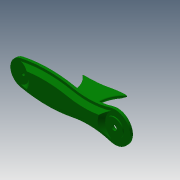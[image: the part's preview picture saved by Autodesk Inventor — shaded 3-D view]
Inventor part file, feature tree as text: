
AUTODESK INVENTOR PART (.ipt)
format: ipt  version: 2013 (Build 170138000, 138)  size: 402,944 bytes
history: native  units: mm
features: extrude x16, sketch x15, chamfer x3, fillet x1
ambient origin geometry x8: Origin, YZ Plane, XZ Plane, XY Plane, X Axis, Y Axis, Z Axis, Center Point
bodies: Solid1 (feature_tree)
feature tree (35):
  extrude  "Extrusion1"  Depth=50.0mm
  extrude  "Extrusion2"  Depth=15.0mm
  extrude  "Extrusion3"  Depth=5.0mm TaperAngle=0.0deg
  extrude  "Extrusion4"  Depth=18.1mm
  extrude  "Extrusion5"  Depth=20.0mm
  extrude  "Extrusion6"  Depth=9.5mm
  sketch  "Sketch7"  dims[d15=9.9mm d16=9.5mm]
  extrude  "Extrusion7"  Depth=9.5mm
  chamfer  "Chamfer1"  Distance=5.0mm
  extrude  "Extrusion8"  Depth=2.0mm
  extrude  "Extrusion17"  Depth=5.0mm TaperAngle=0.0deg
  chamfer  "Chamfer2"  Distance=5.0mm
  extrude  "Extrusion25"  Depth=5.0mm TaperAngle=0.0deg
  extrude  "Extrusion26"  Depth=20.0mm
  extrude  "Extrusion27"  Depth=30.0mm
  sketch  "Sketch30"  dims[d26=2.0mm d29=2.0mm]
  extrude  "Extrusion28"  Depth=7.3mm TaperAngle=0.0deg
  extrude  "Extrusion32"  Depth=7.3mm TaperAngle=45.0deg
  extrude  "Extrusion33"  Depth=12.3mm TaperAngle=0.0deg
  extrude  "Extrusion34"  Depth=6.0mm
  chamfer  "Chamfer3"  Distance=5.0mm
  fillet  "Fillet4"  Radius=7.3mm
  sketch  "Sketch1"  dims[d0=180.0mm d1=50.0mm]
  sketch  "Sketch2"  dims[d2=5.0mm d3=0.0mm d4=15.0mm]
  sketch  "Sketch3"  dims[d5=15.0mm d6=5.0mm d7=0.0mm]
  sketch  "Sketch4"  dims[d9=34.65mm d10=18.1mm]
  sketch  "Sketch5"  dims[d11=55.0mm d12=20.0mm]
  sketch  "Sketch6"  dims[d13=40.2mm d14=9.5mm]
  sketch  "Sketch8"  dims[d17=9.9mm]
  sketch  "Sketch9"  dims[d18=3.0mm]
  sketch  "Sketch18"  dims[d19=3.0mm]
  sketch  "Sketch27"  dims[d20=3.0mm]
  sketch  "Sketch28"  dims[d21=3.0mm]
  sketch  "Sketch29"  dims[d22=13.6mm d23=5.0mm d24=0.0mm]
  sketch  "Sketch33"  dims[d30=2.0mm d31=5.0mm d32=0.0mm d63=5.0mm d64=0.0mm d65=5.0mm d66=0.0mm d72=20.0mm d73=30.0mm d74=7.3mm d75=0.0mm d76=7.3mm d77=2.0mm d78=45.0deg d79=12.3mm d80=0.0mm d114=6.0mm d115=5.0mm d116=0.0mm d117=7.3mm d118=2.0mm d119=45.0deg d155=35.0mm d156=2.0mm d157=0.0mm d158=10.0mm d159=2.0mm d160=0.0mm d161=5.0mm d162=0.0mm d177=72.6mm d178=0.0mm d183=20.0mm d184=80.0mm d192=80.0mm d195=10.0mm d196=20.0mm d197=10.0mm d199=72.6mm d200=0.0mm d201=45.0mm d202=45.0mm d203=20.0mm d204=0.0mm d205=72.6mm d206=0.0mm d207=8.0mm d208=2.0mm d209=45.0deg d210=2.0mm]
